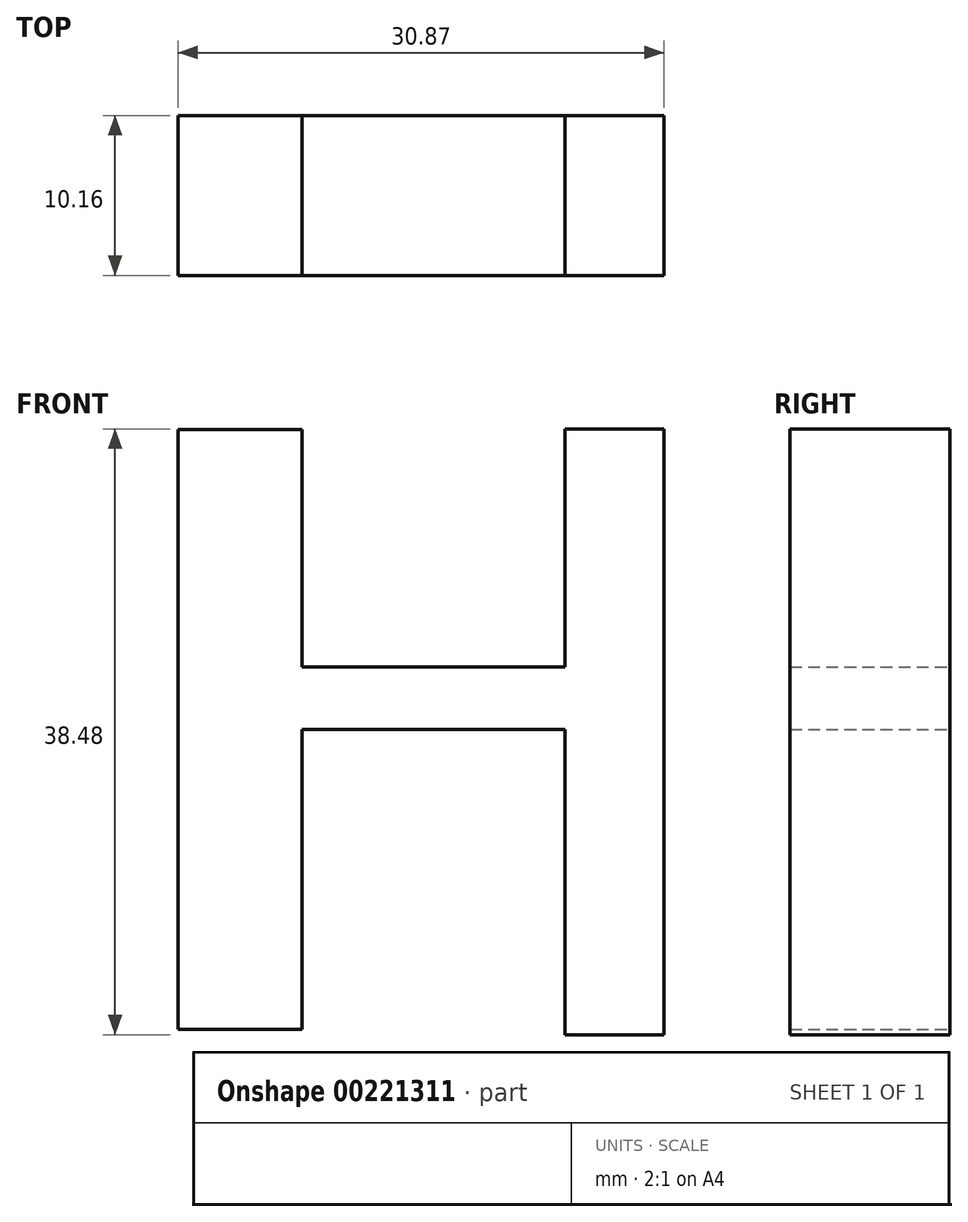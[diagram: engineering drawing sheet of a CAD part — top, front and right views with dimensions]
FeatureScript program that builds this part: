
annotation { "Feature Type Name" : "Feature", "Feature Type Description" : "" }
export const myFeature = defineFeature(function(context is Context, id is Id, definition is map)
    precondition{}
    {
        {
            var Q0;
            Q0=qCreatedBy(makeId("Front.planeOp"),FACE);
            var sketch = newSketch(context, id + "F0", { "sketchPlane" : qUnion([Q0])});
            skLineSegment(sketch, "E0.bottom", {"start": v(-27.75, 26.73) * mm, "end": v(-19.87, 26.73) * mm});
            skLineSegment(sketch, "E0.top", {"start": v(-27.75, -11.38) * mm, "end": v(-19.87, -11.38) * mm});
            skLineSegment(sketch, "E0.left", {"start": v(-27.75, 26.73) * mm, "end": v(-27.75, -11.38) * mm});
            skLineSegment(sketch, "E1.bottom", {"start": v(-3.19, -11.72) * mm, "end": v(3.12, -11.72) * mm});
            skLineSegment(sketch, "E1.top", {"start": v(-3.19, 26.76) * mm, "end": v(3.12, 26.76) * mm});
            skLineSegment(sketch, "E1.right", {"start": v(3.12, -11.72) * mm, "end": v(3.12, 26.76) * mm});
            skLineSegment(sketch, "E2.bottom", {"start": v(-3.19, 11.62) * mm, "end": v(-19.87, 11.62) * mm});
            skLineSegment(sketch, "E2.top", {"start": v(-3.19, 7.67) * mm, "end": v(-19.87, 7.67) * mm});
            skLineSegment(sketch, "E3", {"start": v(-3.19, 11.62) * mm, "end": v(-3.19, 26.76) * mm});
            skLineSegment(sketch, "E4", {"start": v(-3.19, 7.67) * mm, "end": v(-3.19, -11.72) * mm});
            skLineSegment(sketch, "E5", {"start": v(-19.87, -11.38) * mm, "end": v(-19.87, 7.67) * mm});
            skLineSegment(sketch, "E6", {"start": v(-19.87, 11.62) * mm, "end": v(-19.87, 26.73) * mm});
            skSolve(sketch);
        }
        {
            var Q0;
            Q0=makeQuery(id+"F0.imprint","IMPRINT",FACE,{"disambiguationData":[TD([[makeQuery(id+"F0.imprint","IMPRINT",EDGE,{"derivedFrom":sQuery(id+"F0.wireOp",EDGE,"E0.bottom")}),-1.0]])]});
            extrude(context, id + "F1", {"entities" : qUnion([Q0]), "depth" : 10.16 * mm});
        }
    });
